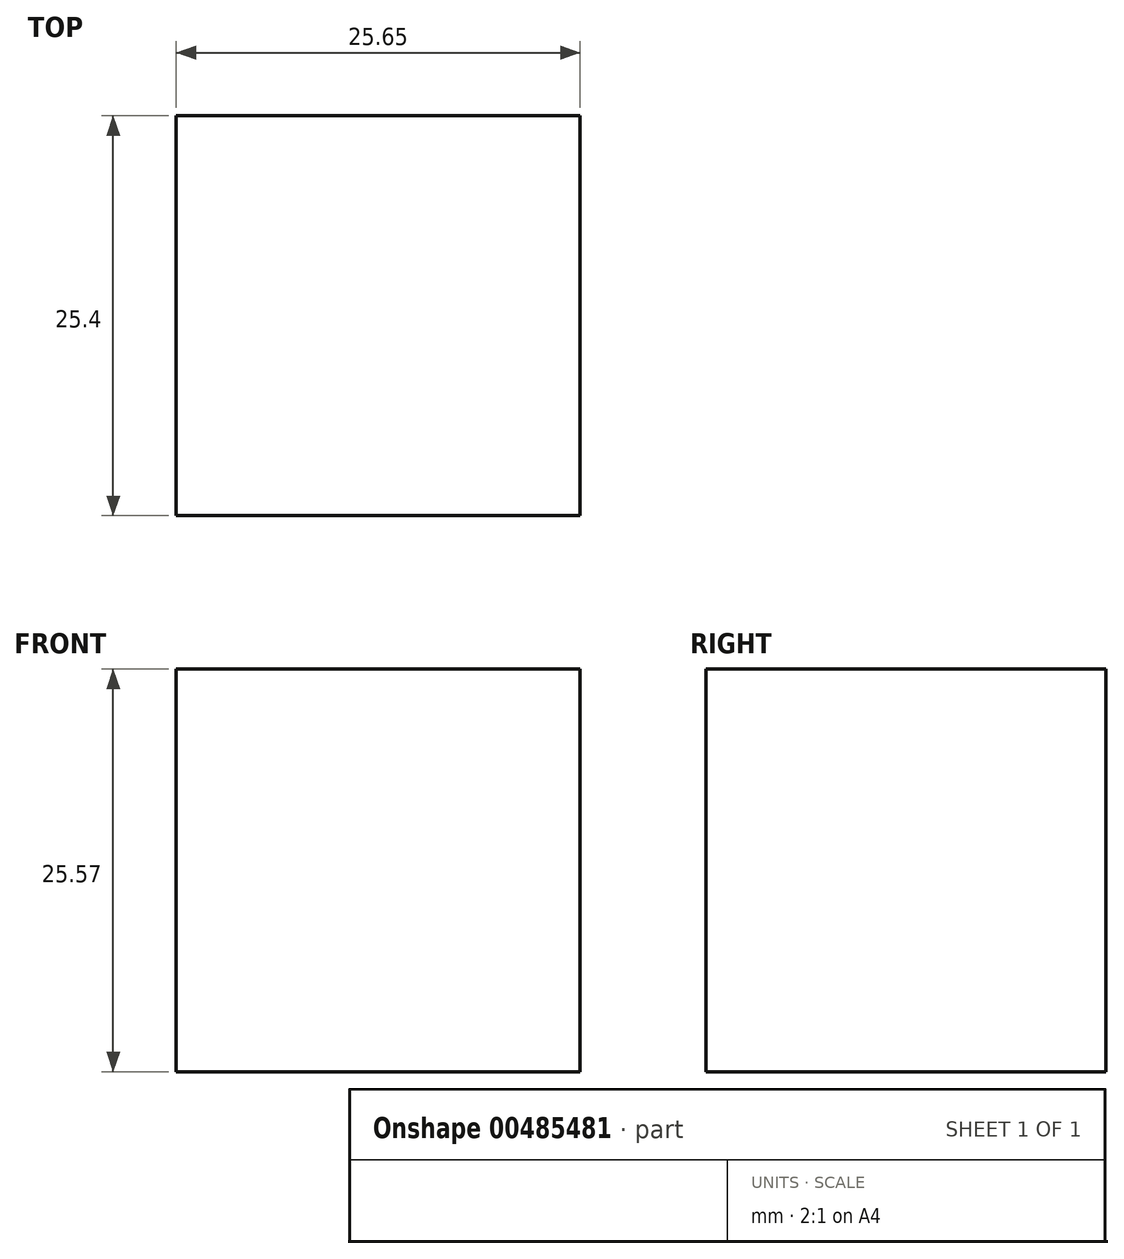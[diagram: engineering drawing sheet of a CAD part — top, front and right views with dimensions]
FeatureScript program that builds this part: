
annotation { "Feature Type Name" : "Feature", "Feature Type Description" : "" }
export const myFeature = defineFeature(function(context is Context, id is Id, definition is map)
    precondition{}
    {
        {
            var Q0;
            Q0=qCreatedBy(makeId("Front.planeOp"),FACE);
            var sketch = newSketch(context, id + "F0", { "sketchPlane" : qUnion([Q0])});
            skLineSegment(sketch, "E0", {"start": v(0, 0) * mm, "end": v(25.33, 0) * mm});
            skLineSegment(sketch, "E1.bottom", {"start": v(0, 0) * mm, "end": v(-25.65, 0) * mm});
            skLineSegment(sketch, "E1.top", {"start": v(0, 25.57) * mm, "end": v(-25.65, 25.57) * mm});
            skLineSegment(sketch, "E1.left", {"start": v(0, 0) * mm, "end": v(0, 25.57) * mm});
            skLineSegment(sketch, "E1.right", {"start": v(-25.65, 0) * mm, "end": v(-25.65, 25.57) * mm});
            skSolve(sketch);
        }
        {
            var Q0;
            Q0=makeQuery(id+"F0.imprint","IMPRINT",FACE,{"disambiguationData":[TD([[makeQuery(id+"F0.imprint","IMPRINT",EDGE,{"derivedFrom":sQuery(id+"F0.wireOp",EDGE,"E1.bottom")}),-1.0]])]});
            extrude(context, id + "F1", {"entities" : qUnion([Q0]), "depth" : 25.4 * mm});
        }
    });
